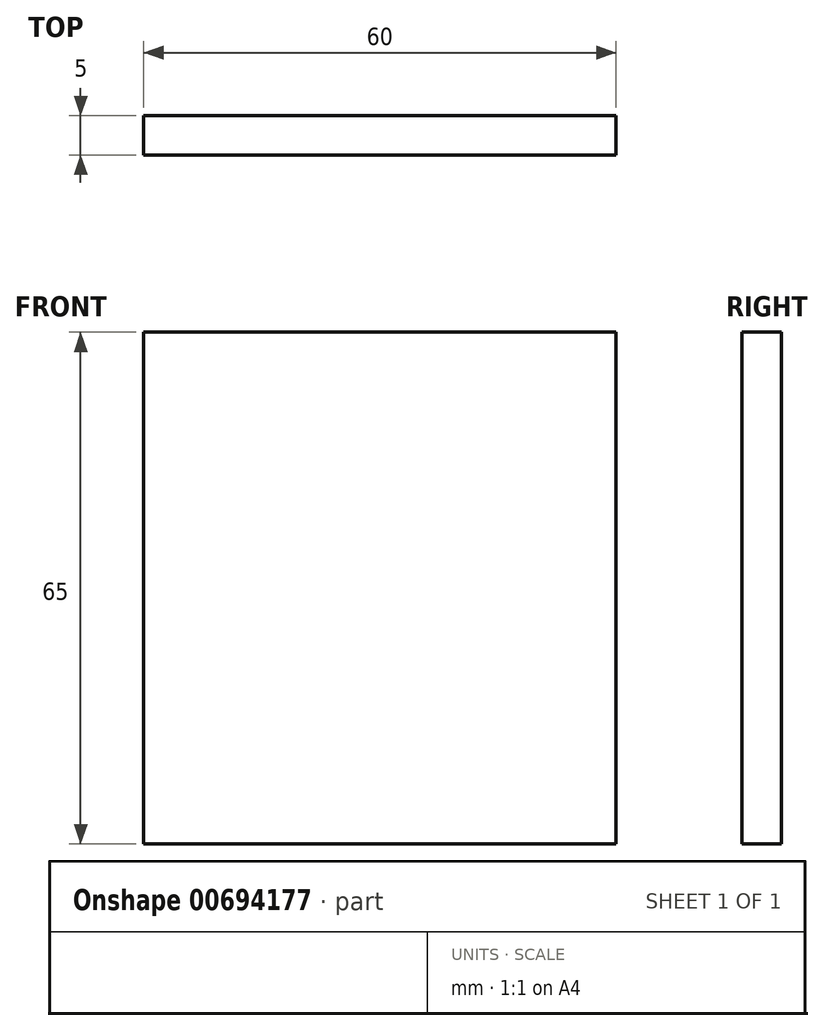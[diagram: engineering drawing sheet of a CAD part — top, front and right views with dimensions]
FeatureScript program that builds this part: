
annotation { "Feature Type Name" : "Feature", "Feature Type Description" : "" }
export const myFeature = defineFeature(function(context is Context, id is Id, definition is map)
    precondition{}
    {
        {
            var Q0;
            Q0=qCreatedBy(makeId("Front.planeOp"),FACE);
            var sketch = newSketch(context, id + "F0", { "sketchPlane" : qUnion([Q0])});
            skLineSegment(sketch, "E0.bottom", {"start": v(-24.43, 35.36) * mm, "end": v(35.57, 35.36) * mm});
            skLineSegment(sketch, "E0.top", {"start": v(-24.43, -29.64) * mm, "end": v(35.57, -29.64) * mm});
            skLineSegment(sketch, "E0.left", {"start": v(-24.43, 35.36) * mm, "end": v(-24.43, -29.64) * mm});
            skLineSegment(sketch, "E0.right", {"start": v(35.57, 35.36) * mm, "end": v(35.57, -29.64) * mm});
            skSolve(sketch);
        }
        {
            var Q0;
            Q0=makeQuery(id+"F0.imprint","IMPRINT",FACE,{"disambiguationData":[TD([[makeQuery(id+"F0.imprint","IMPRINT",EDGE,{"derivedFrom":sQuery(id+"F0.wireOp",EDGE,"E0.bottom")}),-1.0]])]});
            extrude(context, id + "F1", {"entities" : qUnion([Q0]), "depth" : 5 * mm, "offsetDistance" : 25 * mm});
        }
    });
